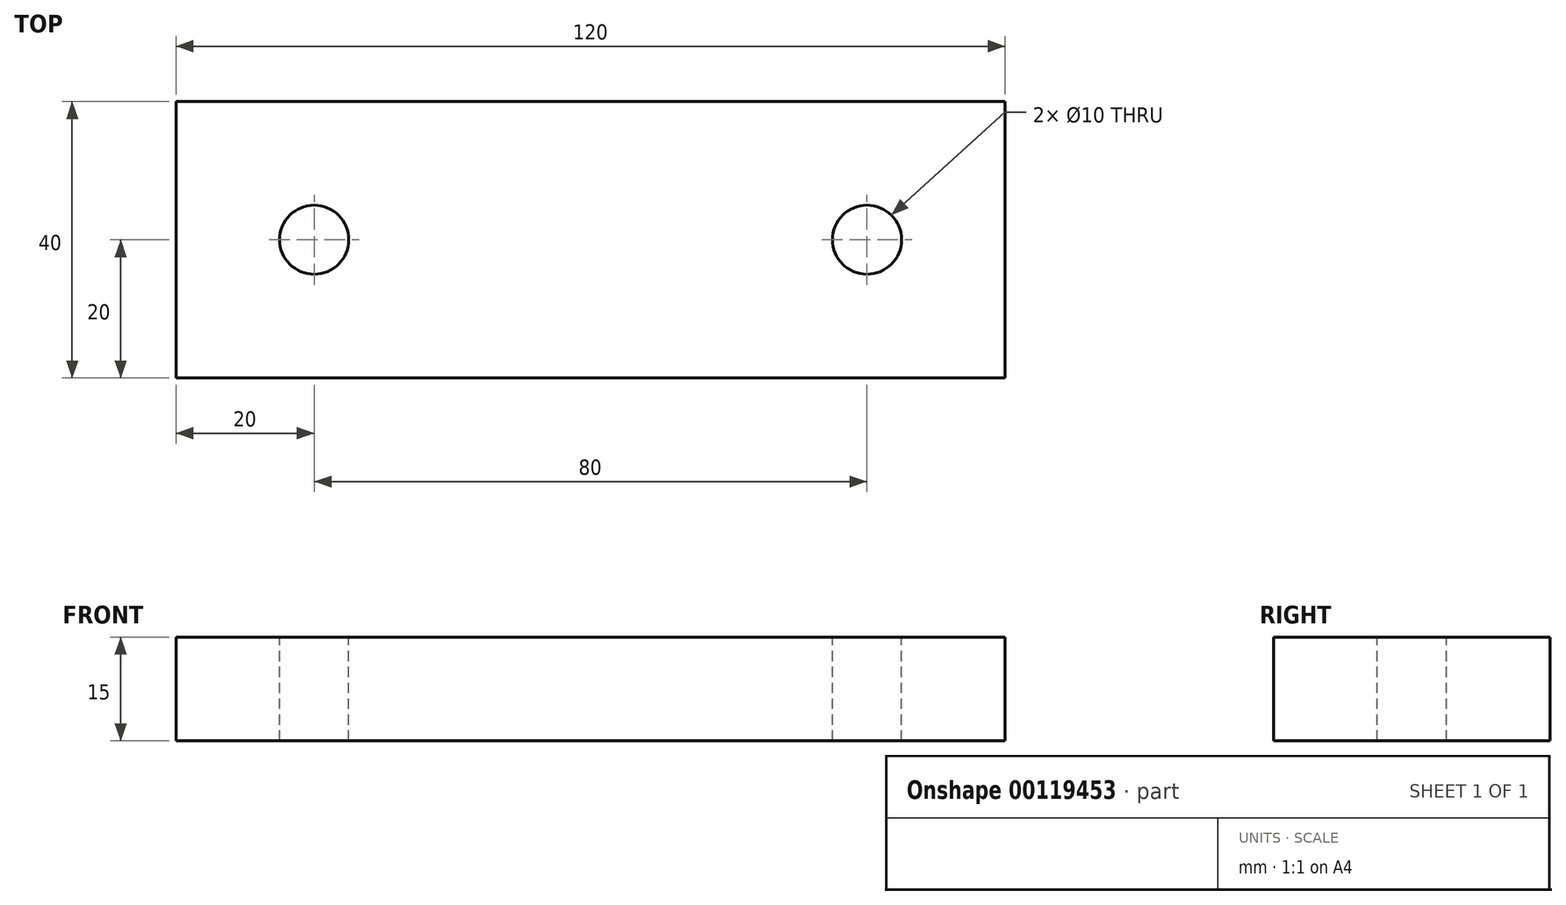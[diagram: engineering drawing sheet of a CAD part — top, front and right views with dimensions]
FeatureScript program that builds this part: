
annotation { "Feature Type Name" : "Feature", "Feature Type Description" : "" }
export const myFeature = defineFeature(function(context is Context, id is Id, definition is map)
    precondition{}
    {
        {
            var Q0;
            Q0=qCreatedBy(makeId("Front.planeOp"),FACE);
            var sketch = newSketch(context, id + "F0", { "sketchPlane" : qUnion([Q0])});
            skLineSegment(sketch, "E0.bottom", {"start": v(60, -7.5) * mm, "end": v(-60, -7.5) * mm});
            skLineSegment(sketch, "E0.top", {"start": v(60, 7.5) * mm, "end": v(-60, 7.5) * mm});
            skLineSegment(sketch, "E0.left", {"start": v(60, -7.5) * mm, "end": v(60, 7.5) * mm});
            skLineSegment(sketch, "E0.right", {"start": v(-60, -7.5) * mm, "end": v(-60, 7.5) * mm});
            skPoint(sketch, "E0.middle", {"position": v(0, 0) * mm});
            skSolve(sketch);
        }
        {
            var Q0;
            Q0=makeQuery(id+"F0.imprint","IMPRINT",FACE,{"disambiguationData":[TD([[makeQuery(id+"F0.imprint","IMPRINT",EDGE,{"derivedFrom":sQuery(id+"F0.wireOp",EDGE,"E0.bottom")}),-1.0]])]});
            extrude(context, id + "F1", {"entities" : qUnion([Q0]), "endBound" : BoundingType.SYMMETRIC, "oppositeDirection" : true, "depth" : 40 * mm});
        }
        {
            var Q0;
            Q0=makeQuery(id+"F1.opExtrude","SWEPT_FACE",FACE,{"disambiguationData":[OSD([sQuery(id+"F0.wireOp",EDGE,"E0.top")])]});
            var sketch = newSketch(context, id + "F2", { "sketchPlane" : qUnion([Q0])});
            skLineSegment(sketch, "E1", {"start": v(-103.16, 0) * mm, "end": v(134.26, 0) * mm, "construction": true});
            skCircle(sketch, "E2", {"center": v(-40, 0) * mm, "radius": 5 * mm});
            skLineSegment(sketch, "E3", {"start": v(0, 30.36) * mm, "end": v(0, -30.74) * mm, "construction": true});
            skPoint(sketch, "E3.endSnap0", {"position": v(0, -20) * mm});
            skCircle(sketch, "E4.MirrorC", {"center": v(40, 0) * mm, "radius": 5 * mm});
            skSolve(sketch);
        }
        {
            var Q0;
            Q0 = qSketchRegion(id + "F2", true);
            extrude(context, id + "F3", {"entities" : qUnion([Q0]), "operationType" : NewBodyOperationType.REMOVE, "endBound" : BoundingType.THROUGH_ALL, "oppositeDirection" : true, "depth" : 25 * mm});
        }
    });
